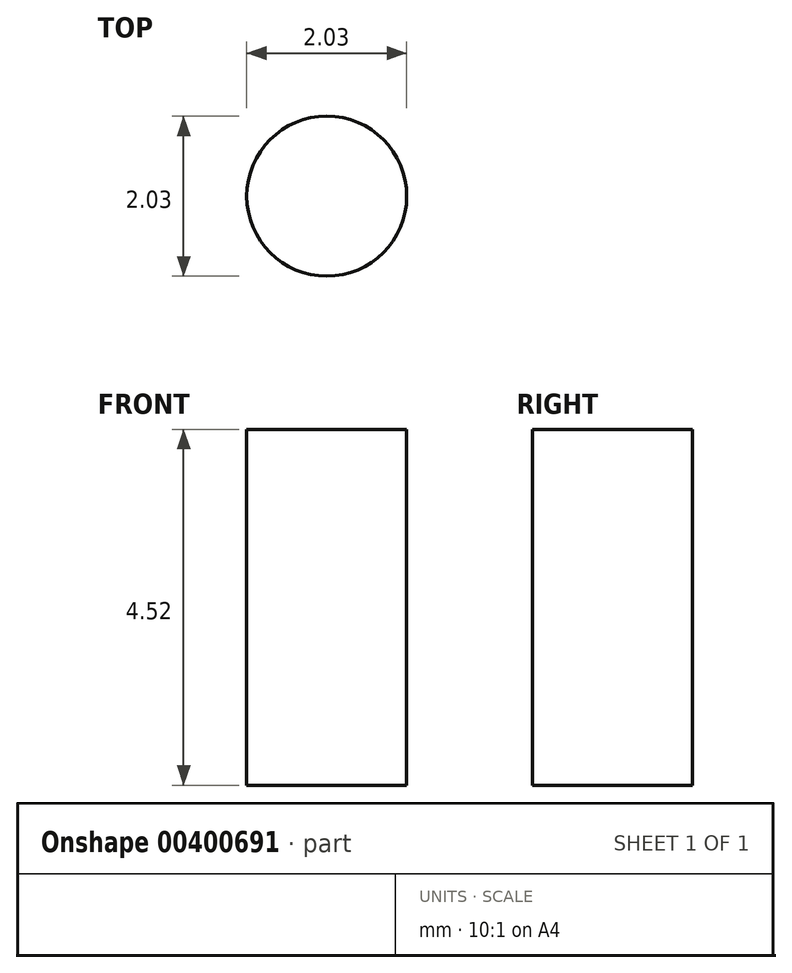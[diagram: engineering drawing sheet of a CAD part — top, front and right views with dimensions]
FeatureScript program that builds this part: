
annotation { "Feature Type Name" : "Feature", "Feature Type Description" : "" }
export const myFeature = defineFeature(function(context is Context, id is Id, definition is map)
    precondition{}
    {
        {
            var Q0;
            Q0=qCreatedBy(makeId("Top.planeOp"),FACE);
            var sketch = newSketch(context, id + "F0", { "sketchPlane" : qUnion([Q0])});
            skCircle(sketch, "E0", {"center": v(-54.44, 36.23) * mm, "radius": 1.02 * mm});
            skSolve(sketch);
        }
        {
            var Q0;
            Q0=makeQuery(id+"F0.imprint","IMPRINT",FACE,{"disambiguationData":[TD([[makeQuery(id+"F0.imprint","IMPRINT",EDGE,{"derivedFrom":sQuery(id+"F0.wireOp",EDGE,"E0")}),1.0]])]});
            extrude(context, id + "F1", {"entities" : qUnion([Q0]), "depth" : 4.52 * mm});
        }
    });
